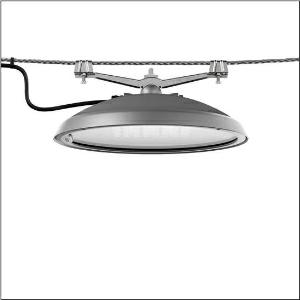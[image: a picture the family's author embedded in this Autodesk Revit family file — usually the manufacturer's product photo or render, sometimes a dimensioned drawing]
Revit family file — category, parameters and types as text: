
# Revit family: dl_r__50_iq_mini___st1_0s_5xa248w21f08ge_9981
name_source: partatom
category: Lighting Fixtures
units: mm (PartAtom-declared; Revit-internal decimal feet)

## family parameters
Cut with Voids When Loaded = No
Host = Face
Light Source = No
Part Type = Normal
Room Calculation Point = No
Round Connector Dimension = Use Diameter
Shared = No

## types (1)
- --- (1 x LED, 4580 lm, 35.2 W, 2200K)
    Apparent Load = 35 VA
    CIE Flux Codes = 37 72 97 100 100
    Color Rendering = 70
    Color Temperature = 2200K
    Default Elevation = 1800 mm
    Description = DL® 50 iQ mini, catenary luminaire, primary light control with lens, of PMMA, primary optical cover: cover, of toughened safety glass, transparent, light distribution: ST1.0s, light emission: direct distribution, primary light characteristic: symmetric, installation type: suspended mounting, LED, High Power LED, rated luminous flux: 4.580lm, luminous efficacy: 130lm/W, light colour: 722, colour temperature: 2200K, control: optimised constant luminous flux control (CLO 2.0), Desk-Remote (wireless, voltage-free reading and setting of iQ features in the workshop via application-optimized NFC function/RFID function), Light-Fading, Smart-Wire, Night-Set, Lumen-Switch, Temp-Guard, Auto-Match, Street-Remote, mains connection: 230..240V, AC, 50/60Hz, start of lifetime: 35W, end of service life: 36W, reduction: 17W, luminaire housing, of diecast aluminium, powder-coated, Siteco® metallic grey (DB 702S), diameter: 500mm, height: 115mm, protection rating (complete): IP66, insulation class (complete): insulation class II (safety insulation), certification: CE, ENEC, VDE, impact resistance: IK08, permissible operating ambient temperature for outdoor applications: -25..+40°C, standard-compliant lighting for roads and squares, packaging unit: 1 piece

Light Distribution: ST1.0s
    Height = 124 mm  [stored 0.406824 ft]
    Lamp = 1 x LED
    Lamp Light Flux = 4580 lm
    Lamp Power = 35.2 W
    Lamp count = 1
    Length = 500 mm
    Luminous efficacy = 130 lm/W
    Manufacturer = Siteco
    ModVariant = No
    Model = 5XA248W21F08GE
    Number of Poles = 1
    OnlyDefault = Yes
    Power Factor = 1
    Product Name = DL® 50 iQ mini | ST1.0s
    Product group = catenary luminaire
    ProductGroupID = 6300
    Protection Class = Protection class II
    Protection Degree = IP 66
    RLX_Detail_Level = 1
    RLX_Emergency_Light_Flux = 0 lm
    RLX_Emergency_Type = 0
    RLX_Emergency_Type_DB = No
    RlxData = <blob elided: 123385 chars, md5=47d52c11>
    Socket = socket
    Standby Power = 0 W
    System Light Flux = 4580 lm
    System Power = 35 W
    Type Comments = factory setting: luminous flux: 100 % | dim-lin: 254 | 365 mA
    Type Image = l_1242791.jpg
    URL = http://relux.com
    VarID = @adj_090275
    Voltage = 0 V
    Weight = 0.00 kg
    Width = 0 mm  [stored 0 ft]

note: [stored X ft] marks values corroborated as IEEE doubles in the binary element streams (Revit-internal decimal feet)

## geometry (parser evidence)
native form markers: Blend x4, Sweep x12
no freeform markers — native parametric forms only
